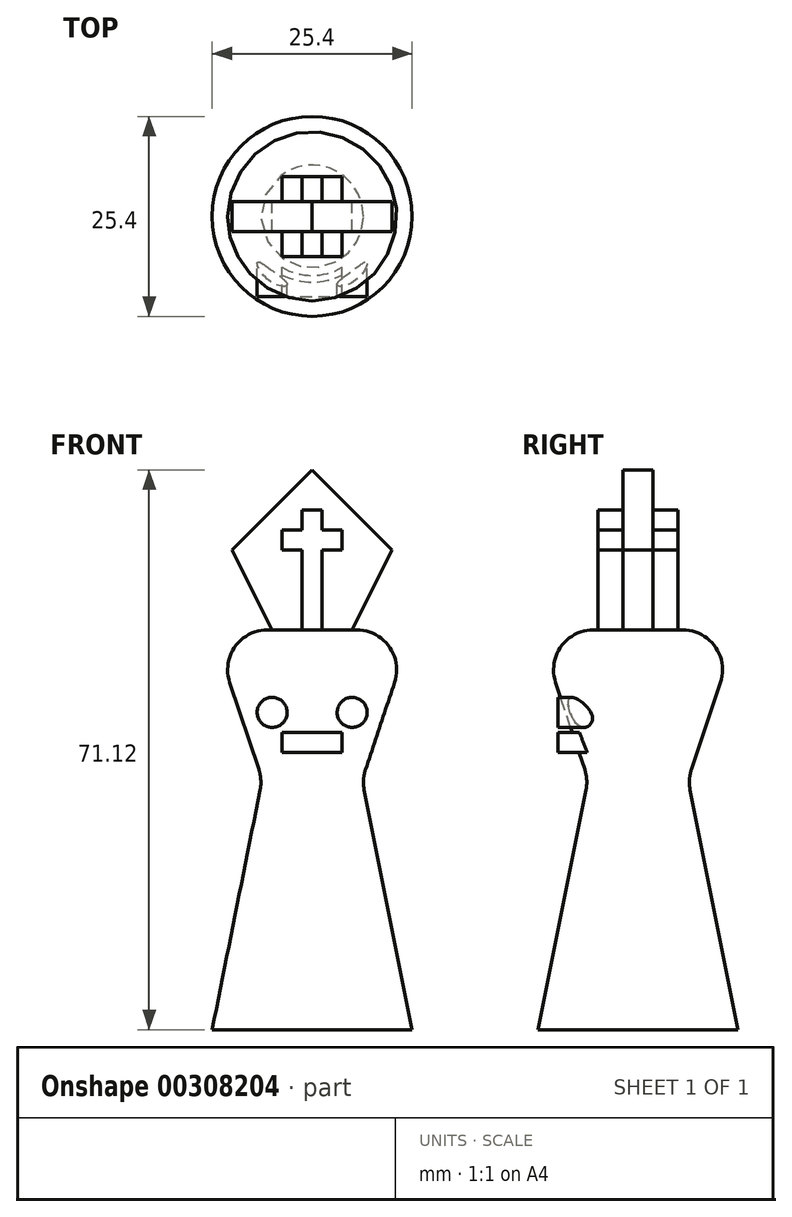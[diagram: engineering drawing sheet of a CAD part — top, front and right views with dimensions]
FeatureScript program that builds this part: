
annotation { "Feature Type Name" : "Feature", "Feature Type Description" : "" }
export const myFeature = defineFeature(function(context is Context, id is Id, definition is map)
    precondition{}
    {
        {
            var Q0;
            Q0=qCreatedBy(makeId("Front.planeOp"),FACE);
            var sketch = newSketch(context, id + "F0", { "sketchPlane" : qUnion([Q0])});
            skLineSegment(sketch, "E0", {"start": v(0, 0) * mm, "end": v(25.4, 0) * mm});
            skLineSegment(sketch, "E1", {"start": v(25.4, 0) * mm, "end": v(19.05, 31.75) * mm});
            skLineSegment(sketch, "E2", {"start": v(19.05, 31.75) * mm, "end": v(25.4, 50.8) * mm});
            skLineSegment(sketch, "E3", {"start": v(25.4, 50.8) * mm, "end": v(0, 50.8) * mm});
            skLineSegment(sketch, "E4", {"start": v(0, 50.8) * mm, "end": v(6.35, 31.75) * mm});
            skLineSegment(sketch, "E5", {"start": v(6.35, 31.75) * mm, "end": v(0, 0) * mm});
            skLineSegment(sketch, "E6", {"start": v(6.35, 31.75) * mm, "end": v(19.05, 31.75) * mm, "construction": true});
            skLineSegment(sketch, "E7", {"start": v(12.7, 50.8) * mm, "end": v(12.7, 0) * mm});
            skPoint(sketch, "E8", {"position": v(12.7, 31.75) * mm});
            skSolve(sketch);
        }
        {
            var Q0;
            {var subQ3=sQuery(id+"F0.wireOp",EDGE,"E1");Q0=makeQuery(id+"F0.imprint","IMPRINT",FACE,{"disambiguationData":[TD([[makeQuery(id+"F0.imprint","IMPRINT",EDGE,{"derivedFrom":subQ3}),1.0]])]});}
            var Q1;
            Q1=sQuery(id+"F0.wireOp",EDGE,"E7");
            revolve(context, id + "F1", {"entities" : qUnion([Q0]), "axis" : qUnion([Q1]), "revolveType" : RevolveType.FULL});
        }
        {
            var Q0;
            Q0=makeQuery(id+"F1.opRevolve","SWEPT_FACE",FACE,{"disambiguationData":[OSD([sQuery(id+"F0.wireOp",EDGE,"E3")])]});
            var Q1;
            Q1=makeQuery(id+"F1.opRevolve","SWEPT_EDGE",EDGE,{"disambiguationData":[OSD([sQuery(id+"F0.wireOp",EDGE,"E1"),sQuery(id+"F0.wireOp",EDGE,"E2")])]});
            fillet(context, id + "F2", {"entities" : qUnion([Q0, Q1]), "radius" : 5.08 * mm, "tangentPropagation" : true, "allowEdgeOverflow" : false});
        }
        {
            var Q0;
            Q0=qCreatedBy(makeId("Front.planeOp"),FACE);
            var sketch = newSketch(context, id + "F3", { "sketchPlane" : qUnion([Q0])});
            skLineSegment(sketch, "E9", {"start": v(7.62, 50.8) * mm, "end": v(17.78, 50.8) * mm});
            skLineSegment(sketch, "E10", {"start": v(17.78, 50.8) * mm, "end": v(22.86, 60.96) * mm});
            skLineSegment(sketch, "E11", {"start": v(22.86, 60.96) * mm, "end": v(12.7, 71.12) * mm});
            skLineSegment(sketch, "E12", {"start": v(12.7, 71.12) * mm, "end": v(2.54, 60.96) * mm});
            skLineSegment(sketch, "E13", {"start": v(2.54, 60.96) * mm, "end": v(7.62, 50.8) * mm});
            skLineSegment(sketch, "E14", {"start": v(12.7, 71.12) * mm, "end": v(12.7, 50.8) * mm, "construction": true});
            skLineSegment(sketch, "E15", {"start": v(2.54, 60.96) * mm, "end": v(22.86, 60.96) * mm, "construction": true});
            skSolve(sketch);
        }
        {
            var Q0;
            Q0=makeQuery(id+"F3.imprint","IMPRINT",FACE,{"disambiguationData":[TD([[makeQuery(id+"F3.imprint","IMPRINT",EDGE,{"derivedFrom":sQuery(id+"F3.wireOp",EDGE,"E9")}),1.0]])]});
            extrude(context, id + "F4", {"entities" : qUnion([Q0]), "operationType" : NewBodyOperationType.ADD, "endBound" : BoundingType.SYMMETRIC, "depth" : 3.8 * mm});
        }
        {
            var Q0;
            Q0=qCreatedBy(makeId("Front.planeOp"),FACE);
            var sketch = newSketch(context, id + "F5", { "sketchPlane" : qUnion([Q0])});
            skLineSegment(sketch, "E16", {"start": v(8.89, 63.5) * mm, "end": v(8.89, 60.96) * mm});
            skLineSegment(sketch, "E17", {"start": v(8.89, 60.96) * mm, "end": v(11.43, 60.96) * mm});
            skLineSegment(sketch, "E18", {"start": v(11.43, 60.96) * mm, "end": v(11.43, 50.8) * mm});
            skLineSegment(sketch, "E19", {"start": v(11.43, 50.8) * mm, "end": v(13.97, 50.8) * mm});
            skLineSegment(sketch, "E20", {"start": v(13.97, 50.8) * mm, "end": v(13.97, 60.96) * mm});
            skLineSegment(sketch, "E21", {"start": v(13.97, 60.96) * mm, "end": v(16.5, 60.96) * mm});
            skLineSegment(sketch, "E22", {"start": v(16.5, 60.96) * mm, "end": v(16.5, 63.5) * mm});
            skLineSegment(sketch, "E23", {"start": v(16.5, 63.5) * mm, "end": v(13.97, 63.5) * mm});
            skLineSegment(sketch, "E24", {"start": v(13.97, 63.5) * mm, "end": v(13.97, 66.04) * mm});
            skLineSegment(sketch, "E25", {"start": v(13.97, 66.04) * mm, "end": v(11.43, 66.04) * mm});
            skLineSegment(sketch, "E26", {"start": v(11.43, 66.04) * mm, "end": v(11.43, 63.5) * mm});
            skLineSegment(sketch, "E27", {"start": v(11.43, 63.5) * mm, "end": v(8.89, 63.5) * mm});
            skLineSegment(sketch, "E28", {"start": v(11.43, 60.96) * mm, "end": v(11.43, 63.5) * mm, "construction": true});
            skLineSegment(sketch, "E29", {"start": v(11.43, 63.5) * mm, "end": v(13.97, 63.5) * mm, "construction": true});
            skLineSegment(sketch, "E30", {"start": v(13.97, 60.96) * mm, "end": v(13.97, 63.5) * mm, "construction": true});
            skLineSegment(sketch, "E31", {"start": v(11.43, 60.96) * mm, "end": v(13.97, 60.96) * mm, "construction": true});
            skLineSegment(sketch, "E32", {"start": v(12.7, 66.04) * mm, "end": v(12.7, 50.8) * mm, "construction": true});
            skSolve(sketch);
        }
        {
            var Q0;
            Q0 = qSketchRegion(id + "F5", true);
            extrude(context, id + "F6", {"entities" : qUnion([Q0]), "operationType" : NewBodyOperationType.ADD, "endBound" : BoundingType.SYMMETRIC, "depth" : 10.16 * mm});
        }
        {
            var Q0;
            Q0=qCreatedBy(makeId("Front.planeOp"),FACE);
            var sketch = newSketch(context, id + "F7", { "sketchPlane" : qUnion([Q0])});
            skCircle(sketch, "E33", {"center": v(7.62, 40.3) * mm, "radius": 1.9 * mm});
            skCircle(sketch, "E34", {"center": v(17.78, 40.3) * mm, "radius": 1.9 * mm});
            skLineSegment(sketch, "E35.bottom", {"start": v(8.89, 37.76) * mm, "end": v(16.5, 37.76) * mm});
            skLineSegment(sketch, "E35.top", {"start": v(8.89, 35.22) * mm, "end": v(16.5, 35.22) * mm});
            skLineSegment(sketch, "E35.left", {"start": v(8.89, 37.76) * mm, "end": v(8.89, 35.22) * mm});
            skLineSegment(sketch, "E35.right", {"start": v(16.5, 37.76) * mm, "end": v(16.5, 35.22) * mm});
            skLineSegment(sketch, "E36", {"start": v(12.7, 44.11) * mm, "end": v(12.7, 37.76) * mm, "construction": true});
            skLineSegment(sketch, "E37", {"start": v(7.62, 40.3) * mm, "end": v(17.78, 40.3) * mm, "construction": true});
            skSolve(sketch);
        }
        {
            var Q0;
            Q0 = qSketchRegion(id + "F7", true);
            extrude(context, id + "F8", {"entities" : qUnion([Q0]), "operationType" : NewBodyOperationType.ADD, "depth" : 10.16 * mm});
        }
    });
